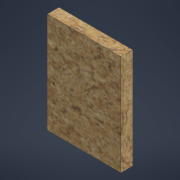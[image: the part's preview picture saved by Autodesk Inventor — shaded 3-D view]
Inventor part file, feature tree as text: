
AUTODESK INVENTOR PART (.ipt)
format: ipt  version: 2022 (Build 260153070, 153G)  size: 117,760 bytes
history: native  units: mm
features: sketch x1, extrude x1
ambient origin geometry x8: Origin, YZ Plane, XZ Plane, XY Plane, X Axis, Y Axis, Z Axis, Center Point
bodies: Body1 (feature_tree)
feature tree (2):
  sketch  "Эскиз1"
  extrude  "Выдавливание2"  Depth=250.0mm
